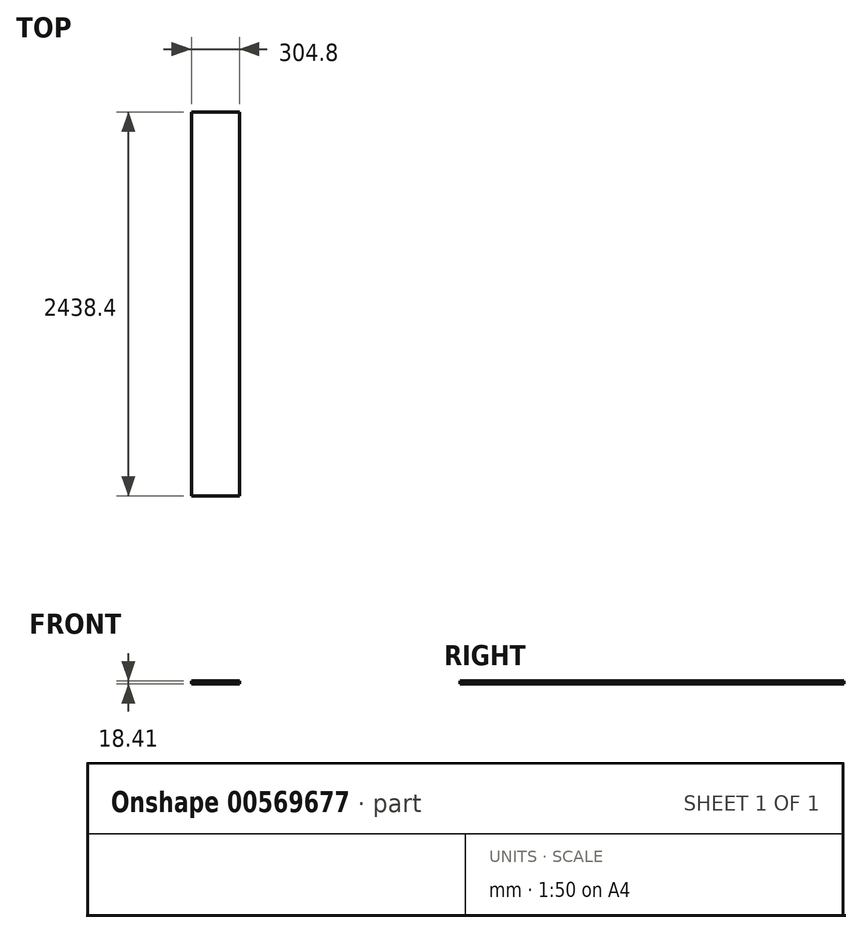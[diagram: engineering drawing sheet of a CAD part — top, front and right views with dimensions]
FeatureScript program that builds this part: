
annotation { "Feature Type Name" : "Feature", "Feature Type Description" : "" }
export const myFeature = defineFeature(function(context is Context, id is Id, definition is map)
    precondition{}
    {
        {
            var Q0;
            Q0=qCreatedBy(makeId("Top.planeOp"),FACE);
            var sketch = newSketch(context, id + "F0", { "sketchPlane" : qUnion([Q0])});
            skLineSegment(sketch, "E0.bottom", {"start": v(-158.78, -290.4) * mm, "end": v(146.02, -290.4) * mm});
            skLineSegment(sketch, "E0.top", {"start": v(-158.78, 2148) * mm, "end": v(146.02, 2148) * mm});
            skLineSegment(sketch, "E0.left", {"start": v(-158.78, -290.4) * mm, "end": v(-158.78, 2148) * mm});
            skLineSegment(sketch, "E0.right", {"start": v(146.02, -290.4) * mm, "end": v(146.02, 2148) * mm});
            skSolve(sketch);
        }
        {
            var Q0;
            Q0 = qSketchRegion(id + "F0", true);
            extrude(context, id + "F1", {"entities" : qUnion([Q0]), "oppositeDirection" : true, "depth" : 18.41 * mm, "offsetDistance" : 25.4 * mm});
        }
    });
